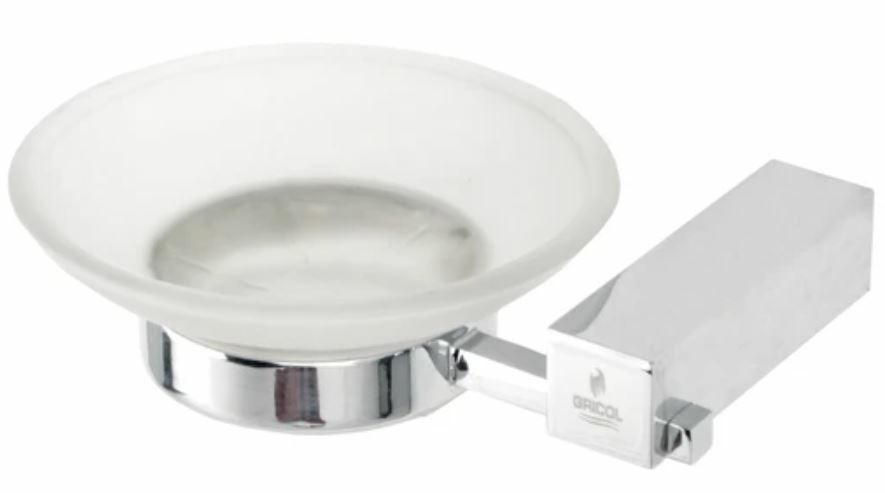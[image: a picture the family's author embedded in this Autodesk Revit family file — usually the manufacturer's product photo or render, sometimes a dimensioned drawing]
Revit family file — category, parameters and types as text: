
# Revit family: 01-2453- 11 JABONERA VIDRIO METALICA QUADRA
name_source: partatom
category: Plumbing Fixtures
revit_build: Autodesk Revit 2018 (Build: 20170223_1515(x64)
units: mm (PartAtom-declared; Revit-internal decimal feet)

## family parameters
Cut with Voids When Loaded = No
Host = Face
OmniClass Number = 23.31.11.00
Part Type = Normal
Room Calculation Point = No
Round Connector Dimension = Use Diameter
Shared = No

## types (1)
- 01-2453-11
    Alto = 37 mm
    Ancho Soporte = 22 mm  [stored 0.0721785 ft]
    Brazo Portacepillos = Metal Laton Cromado
    CW Connection = Yes
    Default Elevation = 0 mm  [stored 0 ft]
    Description = JABONERA
    Diametro vaso = 109 mm  [stored 0.357612 ft]
    HW Connection = Yes
    Jabonera = Vidrio Esmerilado
    Link Ficha Tecnica = http://infotecnica.gricol.com
    Manufacturer = Gricol
    Model = 01-2453- 11
    Product Name = JABONERA VIDRIO METALICA QUADRA
    Profundidad = 75 mm  [stored 0.246063 ft]
    Soporte = Metal Laton Cromado
    Type Image = JABONERA VIDRIO METALICA QUADRA.JPG
    URL = https://www.gricol.com
    Vent Connection = No
    Waste Connection = No

note: [stored X ft] marks values corroborated as IEEE doubles in the binary element streams (Revit-internal decimal feet)

## geometry (parser evidence)
native form markers: Blend x2, Sweep x4
no freeform markers — native parametric forms only
